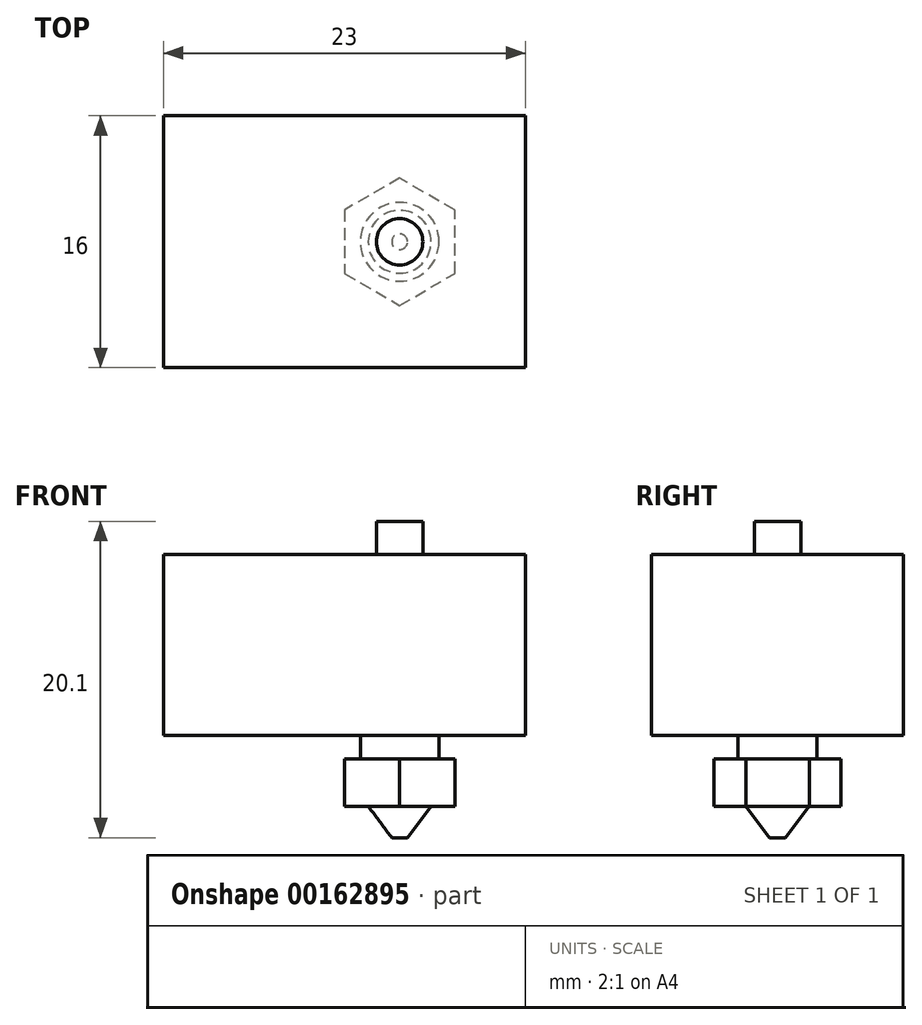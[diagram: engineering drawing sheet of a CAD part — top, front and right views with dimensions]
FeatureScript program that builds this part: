
annotation { "Feature Type Name" : "Feature", "Feature Type Description" : "" }
export const myFeature = defineFeature(function(context is Context, id is Id, definition is map)
    precondition{}
    {
        {
            var Q0;
            Q0=qCreatedBy(makeId("Top.planeOp"),FACE);
            var sketch = newSketch(context, id + "F0", { "sketchPlane" : qUnion([Q0])});
            skCircle(sketch, "E0", {"center": v(0, 0) * mm, "radius": 1.48 * mm});
            skLineSegment(sketch, "E1.bottom", {"start": v(8, -8) * mm, "end": v(-15, -8) * mm});
            skLineSegment(sketch, "E1.top", {"start": v(8, 8) * mm, "end": v(-15, 8) * mm});
            skLineSegment(sketch, "E1.left", {"start": v(8, -8) * mm, "end": v(8, 8) * mm});
            skLineSegment(sketch, "E1.right", {"start": v(-15, -8) * mm, "end": v(-15, 8) * mm});
            skPoint(sketch, "E1.middle", {"position": v(-3.5, 0) * mm});
            skSolve(sketch);
        }
        {
            var Q0;
            Q0=makeQuery(id+"F0.imprint","IMPRINT",FACE,{"disambiguationData":[TD([[makeQuery(id+"F0.imprint","IMPRINT",EDGE,{"derivedFrom":sQuery(id+"F0.wireOp",EDGE,"E0")}),1.0]])]});
            extrude(context, id + "F1", {"entities" : qUnion([Q0]), "depth" : 2.1 * mm, "offsetDistance" : 25 * mm});
        }
        {
            var Q0;
            Q0=makeQuery(id+"F0.imprint","IMPRINT",FACE,{"disambiguationData":[TD([[makeQuery(id+"F0.imprint","IMPRINT",EDGE,{"derivedFrom":sQuery(id+"F0.wireOp",EDGE,"E0")}),-1.0]])]});
            var Q1;
            Q1=makeQuery(id+"F0.imprint","IMPRINT",FACE,{"disambiguationData":[TD([[makeQuery(id+"F0.imprint","IMPRINT",EDGE,{"derivedFrom":sQuery(id+"F0.wireOp",EDGE,"E0")}),1.0]])]});
            extrude(context, id + "F2", {"entities" : qUnion([Q0, Q1]), "oppositeDirection" : true, "depth" : 11.5 * mm, "offsetDistance" : 25 * mm});
        }
        {
            var Q0;
            Q0=makeQuery(id+"F2.opExtrude","CAP_FACE",FACE,{"disambiguationData":[OSD([sQuery(id+"F0.wireOp",EDGE,"E1.bottom"),sQuery(id+"F0.wireOp",EDGE,"E1.top"),sQuery(id+"F0.wireOp",EDGE,"E1.left"),sQuery(id+"F0.wireOp",EDGE,"E1.right")])],"isStart":false});
            var sketch = newSketch(context, id + "F3", { "sketchPlane" : qUnion([Q0])});
            skCircle(sketch, "E2", {"center": v(0, 0) * mm, "radius": 2.5 * mm});
            skSolve(sketch);
        }
        {
            var Q0;
            Q0 = qSketchRegion(id + "F3", true);
            extrude(context, id + "F4", {"entities" : qUnion([Q0]), "operationType" : NewBodyOperationType.ADD, "depth" : 1.5 * mm, "offsetDistance" : 25 * mm});
        }
        {
            var Q0;
            Q0=makeQuery(id+"F4.opExtrude","CAP_FACE",FACE,{"disambiguationData":[OSD([sQuery(id+"F3.wireOp",EDGE,"E2")])],"isStart":false});
            var sketch = newSketch(context, id + "F5", { "sketchPlane" : qUnion([Q0])});
            skCircle(sketch, "E3.cCircle", {"center": v(0, 0) * mm, "radius": 3.5 * mm, "construction": true});
            skLineSegment(sketch, "E3.0", {"start": v(3.5, 2.02) * mm, "end": v(3.5, -2.02) * mm});
            skLineSegment(sketch, "E3.1", {"start": v(3.5, -2.02) * mm, "end": v(0, -4.04) * mm});
            skLineSegment(sketch, "E3.2", {"start": v(0, -4.04) * mm, "end": v(-3.5, -2.02) * mm});
            skLineSegment(sketch, "E3.3", {"start": v(-3.5, -2.02) * mm, "end": v(-3.5, 2.02) * mm});
            skLineSegment(sketch, "E3.4", {"start": v(-3.5, 2.02) * mm, "end": v(0, 4.04) * mm});
            skLineSegment(sketch, "E3.5", {"start": v(0, 4.04) * mm, "end": v(3.5, 2.02) * mm});
            skPoint(sketch, "E3.0.midPoint", {"position": v(3.5, 0) * mm});
            skSolve(sketch);
        }
        {
            var Q0;
            Q0 = qSketchRegion(id + "F5", true);
            extrude(context, id + "F6", {"entities" : qUnion([Q0]), "operationType" : NewBodyOperationType.ADD, "depth" : 3 * mm, "offsetDistance" : 25 * mm});
        }
        {
            var Q0;
            Q0=makeQuery(id+"F6.opExtrude","CAP_FACE",FACE,{"disambiguationData":[OSD([sQuery(id+"F5.wireOp",EDGE,"E3.0"),sQuery(id+"F5.wireOp",EDGE,"E3.1"),sQuery(id+"F5.wireOp",EDGE,"E3.2"),sQuery(id+"F5.wireOp",EDGE,"E3.3"),sQuery(id+"F5.wireOp",EDGE,"E3.4"),sQuery(id+"F5.wireOp",EDGE,"E3.5")])],"isStart":false});
            var sketch = newSketch(context, id + "F7", { "sketchPlane" : qUnion([Q0])});
            skCircle(sketch, "E4", {"center": v(0, 0) * mm, "radius": 2 * mm});
            skSolve(sketch);
        }
        {
            var Q0;
            Q0=makeQuery(id+"F7.imprint","IMPRINT",FACE,{"disambiguationData":[TD([[makeQuery(id+"F7.imprint","IMPRINT",EDGE,{"derivedFrom":sQuery(id+"F7.wireOp",EDGE,"E4")}),-1.0]])]});
            cPlane(context, id + "F8", {"entities" : qUnion([Q0]), "cplaneType" : CPlaneType.OFFSET, "offset" : 2 * mm, "width" : 150 * mm, "height" : 150 * mm});
        }
        {
            var Q0;
            Q0=qCreatedBy(id+"F8.planeOp",FACE);
            var sketch = newSketch(context, id + "F9", { "sketchPlane" : qUnion([Q0])});
            skCircle(sketch, "E5", {"center": v(0, 0) * mm, "radius": 0.5 * mm});
            skSolve(sketch);
        }
        {
            var Q1;
            Q1=makeQuery(id+"F7.imprint","IMPRINT",FACE,{"disambiguationData":[TD([[makeQuery(id+"F7.imprint","IMPRINT",EDGE,{"derivedFrom":sQuery(id+"F7.wireOp",EDGE,"E4")}),1.0]])]});
            var Q2;
            Q2=makeQuery(id+"F9.imprint","IMPRINT",FACE,{"disambiguationData":[TD([[makeQuery(id+"F9.imprint","IMPRINT",EDGE,{"derivedFrom":sQuery(id+"F9.wireOp",EDGE,"E5")}),1.0]])]});
            loft(context, id + "F10", {"operationType" : NewBodyOperationType.ADD, "sheetProfilesArray" : [{ "sheetProfileEntities" : qUnion([Q1]) }, { "sheetProfileEntities" : qUnion([Q2]) }]});
        }
    });
